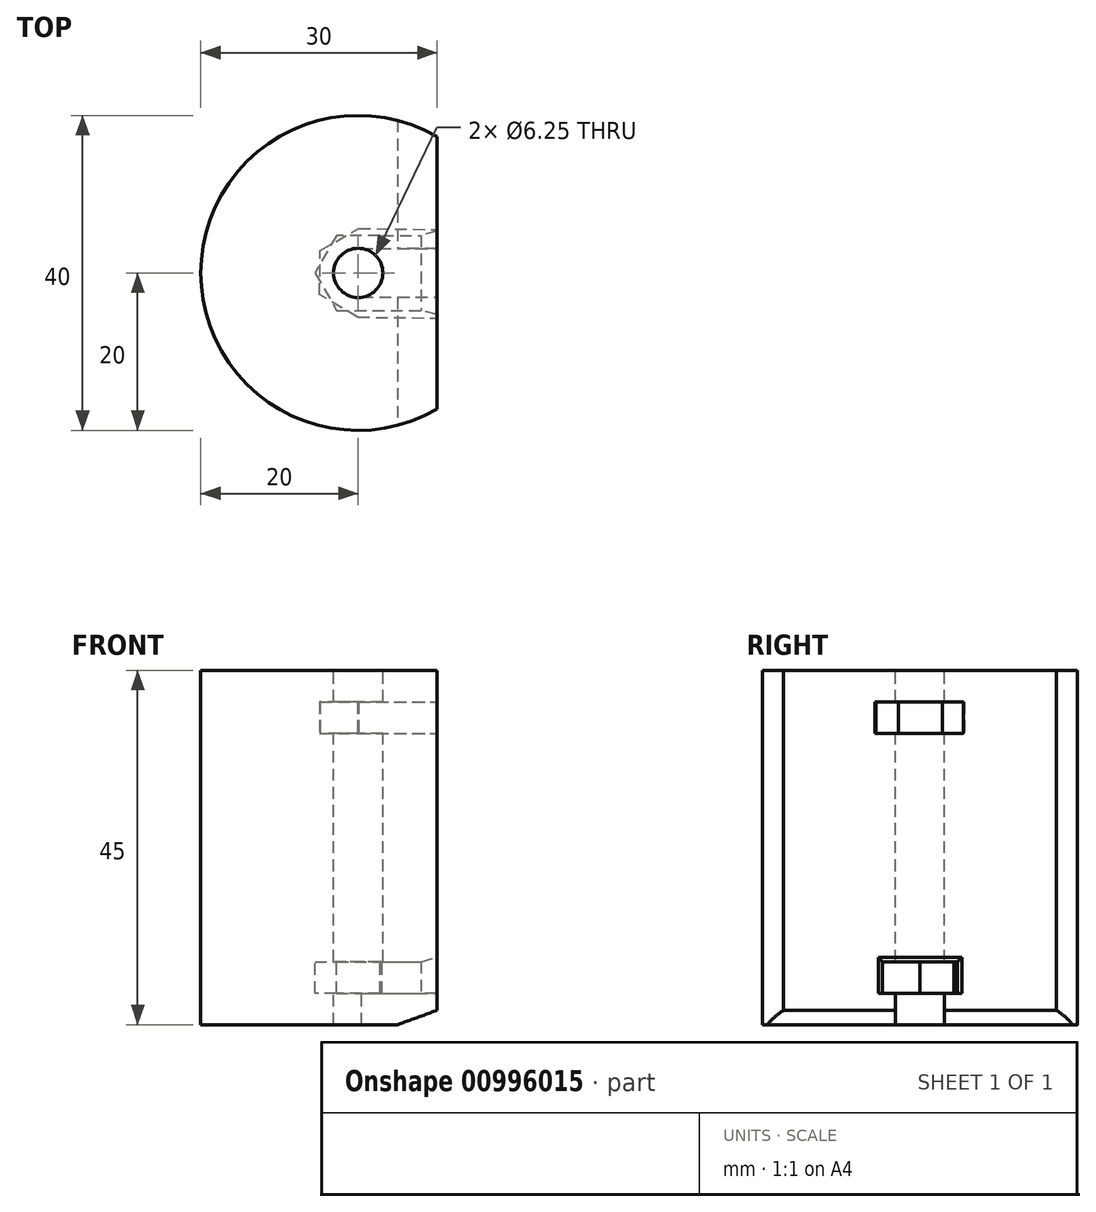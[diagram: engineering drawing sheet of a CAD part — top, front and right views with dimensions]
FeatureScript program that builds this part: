
annotation { "Feature Type Name" : "Feature", "Feature Type Description" : "" }
export const myFeature = defineFeature(function(context is Context, id is Id, definition is map)
    precondition{}
    {
        {
            var Q0;
            Q0=qCreatedBy(makeId("Top.planeOp"),FACE);
            var sketch = newSketch(context, id + "F0", { "sketchPlane" : qUnion([Q0])});
            skCircle(sketch, "E0", {"center": v(0, 0) * mm, "radius": 20 * mm});
            skSolve(sketch);
        }
        {
            var Q0;
            Q0=makeQuery(id+"F0.imprint","IMPRINT",FACE,{"disambiguationData":[TD([[makeQuery(id+"F0.imprint","IMPRINT",EDGE,{"derivedFrom":sQuery(id+"F0.wireOp",EDGE,"E0")}),1.0]])]});
            extrude(context, id + "F1", {"entities" : qUnion([Q0]), "endBound" : BoundingType.SYMMETRIC, "depth" : 45 * mm, "offsetDistance" : 25 * mm});
        }
        {
            var Q0;
            Q0=makeQuery(id+"F1.opExtrude","CAP_FACE",FACE,{"disambiguationData":[OSD([sQuery(id+"F0.wireOp",EDGE,"E0")])],"isStart":false});
            var sketch = newSketch(context, id + "F2", { "sketchPlane" : qUnion([Q0])});
            skCircle(sketch, "E1.cCircle", {"center": v(0, 0) * mm, "radius": 5.62 * mm, "construction": true});
            skLineSegment(sketch, "E1.0", {"start": v(4.9, 2.76) * mm, "end": v(4.84, -2.87) * mm});
            skLineSegment(sketch, "E1.1", {"start": v(4.84, -2.87) * mm, "end": v(-0.06, -5.62) * mm});
            skLineSegment(sketch, "E1.2", {"start": v(-0.06, -5.62) * mm, "end": v(-4.9, -2.76) * mm});
            skLineSegment(sketch, "E1.3", {"start": v(-4.9, -2.76) * mm, "end": v(-4.84, 2.87) * mm});
            skLineSegment(sketch, "E1.4", {"start": v(-4.84, 2.87) * mm, "end": v(0.06, 5.62) * mm});
            skLineSegment(sketch, "E1.5", {"start": v(0.06, 5.62) * mm, "end": v(4.9, 2.76) * mm});
            skLineSegment(sketch, "E2", {"start": v(0.06, 5.62) * mm, "end": v(49.1, 5.09) * mm});
            skLineSegment(sketch, "E3", {"start": v(-0.06, -5.62) * mm, "end": v(49.1, -6.16) * mm});
            skLineSegment(sketch, "E4", {"start": v(49.1, 5.09) * mm, "end": v(49.1, -6.16) * mm});
            skCircle(sketch, "E5", {"center": v(0, 0) * mm, "radius": 3.12 * mm});
            skLineSegment(sketch, "E6", {"start": v(10, 23.77) * mm, "end": v(10, -27.14) * mm});
            skLineSegment(sketch, "E7", {"start": v(10, -27.14) * mm, "end": v(69.74, 0) * mm});
            skLineSegment(sketch, "E8", {"start": v(69.74, 0) * mm, "end": v(10, 23.77) * mm});
            skSolve(sketch);
        }
        {
            var Q0;
            Q0=makeQuery(id+"F2.imprint","IMPRINT",FACE,{"disambiguationData":[TD([[makeQuery(id+"F2.imprint","IMPRINT",EDGE,{"derivedFrom":sQuery(id+"F2.wireOp",EDGE,"E1.0")}),-1.0]])]});
            var Q1;
            Q1=makeQuery(id+"F2.imprint","IMPRINT",FACE,{"disambiguationData":[TD([[makeQuery(id+"F2.imprint","IMPRINT",EDGE,{"derivedFrom":sQuery(id+"F2.wireOp",EDGE,"E1.0")}),1.0]])]});
            var Q2;
            {var subQ0=sQuery(id+"F2.wireOp",EDGE,"E4");Q2=makeQuery(id+"F2.imprint","IMPRINT",FACE,{"disambiguationData":[TD([[makeQuery(id+"F2.imprint","IMPRINT",EDGE,{"derivedFrom":subQ0}),-1.0]])]});}
            var Q3;
            Q3=makeQuery(id+"F2.imprint","IMPRINT",FACE,{"disambiguationData":[TD([[makeQuery(id+"F2.imprint","IMPRINT",EDGE,{"derivedFrom":sQuery(id+"F2.wireOp",EDGE,"E5")}),1.0]])]});
            extrude(context, id + "F3", {"entities" : qUnion([Q0, Q1, Q2, Q3]), "depth" : 4 * mm, "offsetDistance" : 25 * mm});
        }
        {
            var Q0;
            Q0=makeQuery(id+"F3.opExtrude","SWEPT_BODY",BODY,{"disambiguationData":[OSD([sQuery(id+"F2.wireOp",EDGE,"E1.0"),sQuery(id+"F2.wireOp",EDGE,"E1.1"),sQuery(id+"F2.wireOp",EDGE,"E1.2"),sQuery(id+"F2.wireOp",EDGE,"E1.3"),sQuery(id+"F2.wireOp",EDGE,"E1.4"),sQuery(id+"F2.wireOp",EDGE,"E1.5")])]});
            var Q1;
            Q1=makeQuery(id+"F1.opExtrude","CAP_FACE",FACE,{"disambiguationData":[OSD([sQuery(id+"F0.wireOp",EDGE,"E0")])],"isStart":true});
            transform(context, id + "F4", {"entities" : qUnion([Q0]), "transformType" : TransformType.TRANSLATION_DISTANCE, "transformDirection" : qUnion([Q1]), "distance" : 8 * mm, "makeCopy" : false});
        }
        {
            var Q0;
            Q0=makeQuery(id+"F2.imprint","IMPRINT",FACE,{"disambiguationData":[TD([[makeQuery(id+"F2.imprint","IMPRINT",EDGE,{"derivedFrom":sQuery(id+"F2.wireOp",EDGE,"E5")}),1.0]])]});
            var Q1;
            {var subQ0=sQuery(id+"F2.wireOp",EDGE,"E6");var subQ1=sQuery(id+"F2.wireOp",EDGE,"E2");var subQ2=makeQuery(id+"F2.imprint","INTERSECT",VERTEX,{"derivedFrom":[subQ1,subQ0]});Q1=makeQuery(id+"F2.imprint","IMPRINT",FACE,{"disambiguationData":[TD([[makeQuery(id+"F2.imprint","IMPRINT",EDGE,{"disambiguationData":[TD([[subQ2,-1.0]])],"derivedFrom":subQ1}),1.0]])]});}
            var Q2;
            {var subQ0=sQuery(id+"F2.wireOp",EDGE,"E6");var subQ1=sQuery(id+"F2.wireOp",EDGE,"E2");var subQ2=makeQuery(id+"F2.imprint","INTERSECT",VERTEX,{"derivedFrom":[subQ1,subQ0]});Q2=makeQuery(id+"F2.imprint","IMPRINT",FACE,{"disambiguationData":[TD([[makeQuery(id+"F2.imprint","IMPRINT",EDGE,{"disambiguationData":[TD([[subQ2,-1.0]])],"derivedFrom":subQ1}),-1.0]])]});}
            var Q3;
            {var subQ0=sQuery(id+"F2.wireOp",EDGE,"E6");var subQ1=sQuery(id+"F2.wireOp",EDGE,"E3");var subQ2=makeQuery(id+"F2.imprint","INTERSECT",VERTEX,{"derivedFrom":[subQ1,subQ0]});Q3=makeQuery(id+"F2.imprint","IMPRINT",FACE,{"disambiguationData":[TD([[makeQuery(id+"F2.imprint","IMPRINT",EDGE,{"disambiguationData":[TD([[subQ2,-1.0]])],"derivedFrom":subQ1}),-1.0]])]});}
            extrude(context, id + "F5", {"entities" : qUnion([Q0, Q1, Q2, Q3]), "operationType" : NewBodyOperationType.REMOVE, "endBound" : BoundingType.THROUGH_ALL, "oppositeDirection" : true, "depth" : 25 * mm, "offsetDistance" : 25 * mm});
        }
        {
            var Q0;
            Q0=makeQuery(id+"F3.opExtrude","SWEPT_BODY",BODY,{"disambiguationData":[OSD([sQuery(id+"F0.wireOp",EDGE,"E0"),sQuery(id+"F2.wireOp",EDGE,"E2"),sQuery(id+"F2.wireOp",EDGE,"E3"),sQuery(id+"F2.wireOp",EDGE,"E4")])]});
            deleteBodies(context, id + "F6", {"entities" : qUnion([Q0])});
        }
        {
            var Q0;
            Q0=makeQuery(id+"F3.opExtrude","SWEPT_BODY",BODY,{"disambiguationData":[OSD([sQuery(id+"F2.wireOp",EDGE,"E1.2"),sQuery(id+"F2.wireOp",EDGE,"E1.3"),sQuery(id+"F2.wireOp",EDGE,"E1.4"),sQuery(id+"F2.wireOp",EDGE,"E2"),sQuery(id+"F2.wireOp",EDGE,"E3"),sQuery(id+"F2.wireOp",EDGE,"E6")])]});
            var Q1;
            Q1=makeQuery(id+"F1.opExtrude","SWEPT_BODY",BODY,{"disambiguationData":[OSD([sQuery(id+"F0.wireOp",EDGE,"E0")])]});
            booleanBodies(context, id + "F7", {"operationType" : BooleanOperationType.SUBTRACTION, "tools" : qUnion([Q0]), "targets" : qUnion([Q1])});
        }
        {
            var Q0;
            Q0=makeQuery(id+"F1.opExtrude","CAP_FACE",FACE,{"disambiguationData":[OSD([sQuery(id+"F0.wireOp",EDGE,"E0")])],"isStart":true});
            var sketch = newSketch(context, id + "F8", { "sketchPlane" : qUnion([Q0])});
            skCircle(sketch, "E9.cCircle", {"center": v(0, 0) * mm, "radius": 5.5 * mm, "construction": true});
            skLineSegment(sketch, "E9.0", {"start": v(5.5, 0) * mm, "end": v(2.75, -4.76) * mm});
            skLineSegment(sketch, "E9.1", {"start": v(2.75, -4.76) * mm, "end": v(-2.75, -4.76) * mm});
            skLineSegment(sketch, "E9.2", {"start": v(-2.75, -4.76) * mm, "end": v(-5.5, 0) * mm});
            skLineSegment(sketch, "E9.3", {"start": v(-5.5, 0) * mm, "end": v(-2.75, 4.76) * mm});
            skLineSegment(sketch, "E9.4", {"start": v(-2.75, 4.76) * mm, "end": v(2.75, 4.76) * mm});
            skLineSegment(sketch, "E9.5", {"start": v(2.75, 4.76) * mm, "end": v(5.5, 0) * mm});
            skLineSegment(sketch, "E10", {"start": v(0, 0) * mm, "end": v(0, -21.96) * mm, "construction": true});
            skLineSegment(sketch, "E11", {"start": v(3, -21.96) * mm, "end": v(3, 0) * mm});
            skLineSegment(sketch, "E12.MirrorCS", {"start": v(-3, -21.96) * mm, "end": v(-3, 0) * mm});
            skLineSegment(sketch, "E13", {"start": v(2.75, 4.76) * mm, "end": v(22.17, 4.76) * mm});
            skLineSegment(sketch, "E14", {"start": v(2.75, -4.76) * mm, "end": v(22.86, -4.76) * mm});
            skLineSegment(sketch, "E15", {"start": v(22.86, -4.76) * mm, "end": v(22.17, 4.76) * mm});
            skSolve(sketch);
        }
        {
            var Q0;
            {var subQ0=sQuery(id+"F8.wireOp",EDGE,"E15");Q0=makeQuery(id+"F8.imprint","IMPRINT",FACE,{"disambiguationData":[TD([[makeQuery(id+"F8.imprint","IMPRINT",EDGE,{"derivedFrom":subQ0}),1.0]])]});}
            var Q1;
            {var subQ1=sQuery(id+"F8.wireOp",EDGE,"E9.5");Q1=makeQuery(id+"F8.imprint","IMPRINT",FACE,{"disambiguationData":[TD([[makeQuery(id+"F8.imprint","IMPRINT",EDGE,{"derivedFrom":subQ1}),1.0]])]});}
            var Q2;
            {var subQ0=sQuery(id+"F8.wireOp",EDGE,"E9.3");Q2=makeQuery(id+"F8.imprint","IMPRINT",FACE,{"disambiguationData":[TD([[makeQuery(id+"F8.imprint","IMPRINT",EDGE,{"derivedFrom":subQ0}),-1.0]])]});}
            var Q3;
            {var subQ6=sQuery(id+"F8.wireOp",EDGE,"E9.1");Q3=makeQuery(id+"F8.imprint","IMPRINT",FACE,{"disambiguationData":[TD([[makeQuery(id+"F8.imprint","IMPRINT",EDGE,{"derivedFrom":subQ6}),-1.0]])]});}
            extrude(context, id + "F9", {"entities" : qUnion([Q0, Q1, Q2, Q3]), "depth" : 4 * mm, "offsetDistance" : 25 * mm});
        }
        {
            var Q0;
            Q0=makeQuery(id+"F9.opExtrude","SWEPT_BODY",BODY,{"disambiguationData":[OSD([sQuery(id+"F0.wireOp",EDGE,"E0"),sQuery(id+"F2.wireOp",EDGE,"E5"),sQuery(id+"F8.wireOp",EDGE,"E9.0"),sQuery(id+"F8.wireOp",EDGE,"E9.1"),sQuery(id+"F8.wireOp",EDGE,"E9.2"),sQuery(id+"F8.wireOp",EDGE,"E9.3"),sQuery(id+"F8.wireOp",EDGE,"E9.4"),sQuery(id+"F8.wireOp",EDGE,"E11"),sQuery(id+"F8.wireOp",EDGE,"E13"),sQuery(id+"F8.wireOp",EDGE,"E14"),sQuery(id+"F8.wireOp",EDGE,"E15")])]});
            transform(context, id + "F10", {"entities" : qUnion([Q0]), "transformType" : TransformType.TRANSLATION_3D, "dx" : 0 * mm, "dy" : 0 * mm, "dz" : 8 * mm, "makeCopy" : false});
        }
        {
            var Q0;
            Q0=makeQuery(id+"F9.opExtrude","SWEPT_BODY",BODY,{"disambiguationData":[OSD([sQuery(id+"F0.wireOp",EDGE,"E0"),sQuery(id+"F2.wireOp",EDGE,"E5"),sQuery(id+"F8.wireOp",EDGE,"E9.0"),sQuery(id+"F8.wireOp",EDGE,"E9.1"),sQuery(id+"F8.wireOp",EDGE,"E9.2"),sQuery(id+"F8.wireOp",EDGE,"E9.3"),sQuery(id+"F8.wireOp",EDGE,"E9.4"),sQuery(id+"F8.wireOp",EDGE,"E11"),sQuery(id+"F8.wireOp",EDGE,"E13"),sQuery(id+"F8.wireOp",EDGE,"E14"),sQuery(id+"F8.wireOp",EDGE,"E15")])]});
            var Q1;
            Q1=makeQuery(id+"F1.opExtrude","SWEPT_BODY",BODY,{"disambiguationData":[OSD([sQuery(id+"F0.wireOp",EDGE,"E0")])]});
            booleanBodies(context, id + "F11", {"operationType" : BooleanOperationType.SUBTRACTION, "tools" : qUnion([Q0]), "targets" : qUnion([Q1])});
        }
        {
            var Q0;
            Q0=makeQuery(id+"F5.boolean.opBoolean","COPY",FACE,{"derivedFrom":makeQuery(id+"F5.opExtrude","SWEPT_FACE",FACE,{"disambiguationData":[OSD([sQuery(id+"F2.wireOp",EDGE,"E6")])]})});
            var sketch = newSketch(context, id + "F12", { "sketchPlane" : qUnion([Q0])});
            skLineSegment(sketch, "E16", {"start": v(0, 0) * mm, "end": v(0, -32.34) * mm, "construction": true});
            skPoint(sketch, "E16.endSnap0", {"position": v(0, -22.5) * mm});
            skLineSegment(sketch, "E17", {"start": v(3.1, 0) * mm, "end": v(3.1, -32.34) * mm});
            skLineSegment(sketch, "E18.MirrorCS", {"start": v(-3.1, 0) * mm, "end": v(-3.1, -32.34) * mm});
            skLineSegment(sketch, "E19", {"start": v(-3.1, 0) * mm, "end": v(3.1, 0) * mm});
            skLineSegment(sketch, "E20", {"start": v(-3.1, -32.34) * mm, "end": v(3.1, -32.34) * mm});
            skLineSegment(sketch, "E21", {"start": v(-3.1, -14.5) * mm, "end": v(3.1, -14.5) * mm});
            skSolve(sketch);
        }
        {
            var Q0;
            {var subQ0=sQuery(id+"F12.wireOp",EDGE,"E17");var subQ1=makeQuery(id+"F5.opExtrude","SWEPT_FACE",FACE,{"disambiguationData":[OSD([sQuery(id+"F2.wireOp",EDGE,"E6")])]});var subQ2=sQuery(id+"F0.wireOp",EDGE,"E0");var subQ3=makeQuery(id+"F5.boolean.opBoolean","INTERSECT",EDGE,{"derivedFrom":[makeQuery(id+"F1.opExtrude","CAP_FACE",FACE,{"disambiguationData":[OSD([subQ2])],"isStart":true}),subQ1]});var subQ4=makeQuery(id+"F12.imprint","INTERSECT",VERTEX,{"derivedFrom":[subQ3,subQ0]});Q0=makeQuery(id+"F12.imprint","IMPRINT",FACE,{"disambiguationData":[TD([[makeQuery(id+"F12.imprint","IMPRINT",EDGE,{"disambiguationData":[TD([[subQ4,-1.0]])],"derivedFrom":subQ3}),-1.0]])]});}
            extrude(context, id + "F13", {"entities" : qUnion([Q0]), "operationType" : NewBodyOperationType.REMOVE, "oppositeDirection" : true, "depth" : 10 * mm, "offsetDistance" : 25 * mm});
        }
        {
            var Q0;
            {var subQ0=sQuery(id+"F0.wireOp",EDGE,"E0");var subQ1=makeQuery(id+"F1.opExtrude","CAP_FACE",FACE,{"disambiguationData":[OSD([subQ0])],"isStart":true});var subQ2=makeQuery(id+"F5.opExtrude","SWEPT_FACE",FACE,{"disambiguationData":[OSD([sQuery(id+"F2.wireOp",EDGE,"E6")])]});Q0=makeQuery(id+"F13.boolean.opBoolean","SPLIT",EDGE,{"disambiguationData":[TD([makeQuery(id+"F13.opExtrude","SWEPT_FACE",FACE,{"disambiguationData":[OSD([sQuery(id+"F12.wireOp",EDGE,"E18.MirrorCS")])]})])],"derivedFrom":makeQuery(id+"F5.boolean.opBoolean","INTERSECT",EDGE,{"derivedFrom":[subQ1,subQ2]})});}
            var Q1;
            {var subQ0=sQuery(id+"F0.wireOp",EDGE,"E0");var subQ1=makeQuery(id+"F1.opExtrude","CAP_FACE",FACE,{"disambiguationData":[OSD([subQ0])],"isStart":true});var subQ2=makeQuery(id+"F5.opExtrude","SWEPT_FACE",FACE,{"disambiguationData":[OSD([sQuery(id+"F2.wireOp",EDGE,"E6")])]});Q1=makeQuery(id+"F13.boolean.opBoolean","SPLIT",EDGE,{"disambiguationData":[TD([makeQuery(id+"F13.opExtrude","SWEPT_FACE",FACE,{"disambiguationData":[OSD([sQuery(id+"F12.wireOp",EDGE,"E17")])]})])],"derivedFrom":makeQuery(id+"F5.boolean.opBoolean","INTERSECT",EDGE,{"derivedFrom":[subQ1,subQ2]})});}
            var Q2;
            Q2=makeQuery(id+"F5.boolean.opBoolean","COPY",EDGE,{"derivedFrom":makeQuery(id+"F5.opExtrude","CAP_EDGE",EDGE,{"disambiguationData":[OSD([sQuery(id+"F2.wireOp",EDGE,"E6")])],"isStart":true})});
            chamfer(context, id + "F14", {"entities" : qUnion([Q0, Q1, Q2]), "chamferType" : ChamferType.OFFSET_ANGLE, "width" : 5 * mm, "oppositeDirection" : false, "angle" : 20 * degree, "tangentPropagation" : true});
        }
        {
            var Q0;
            Q0=makeQuery(id+"F11.opBoolean","INTERSECT",EDGE,{"derivedFrom":[makeQuery(id+"F5.boolean.opBoolean","COPY",FACE,{"derivedFrom":makeQuery(id+"F5.opExtrude","SWEPT_FACE",FACE,{"disambiguationData":[OSD([sQuery(id+"F2.wireOp",EDGE,"E6")])]})}),makeQuery(id+"F9.opExtrude","CAP_FACE",FACE,{"disambiguationData":[OSD([sQuery(id+"F0.wireOp",EDGE,"E0"),sQuery(id+"F2.wireOp",EDGE,"E5"),sQuery(id+"F8.wireOp",EDGE,"E9.0"),sQuery(id+"F8.wireOp",EDGE,"E9.1"),sQuery(id+"F8.wireOp",EDGE,"E9.2"),sQuery(id+"F8.wireOp",EDGE,"E9.3"),sQuery(id+"F8.wireOp",EDGE,"E9.4"),sQuery(id+"F8.wireOp",EDGE,"E11"),sQuery(id+"F8.wireOp",EDGE,"E13"),sQuery(id+"F8.wireOp",EDGE,"E14"),sQuery(id+"F8.wireOp",EDGE,"E15")])],"isStart":true})]});
            var Q1;
            Q1=makeQuery(id+"F7.opBoolean","COPY",EDGE,{"derivedFrom":makeQuery(id+"F3.opExtrude","CAP_EDGE",EDGE,{"disambiguationData":[OSD([sQuery(id+"F2.wireOp",EDGE,"E6")])],"isStart":true})});
            var Q2;
            Q2=makeQuery(id+"F7.opBoolean","COPY",EDGE,{"derivedFrom":makeQuery(id+"F3.opExtrude","SWEPT_EDGE",EDGE,{"disambiguationData":[OSD([sQuery(id+"F2.wireOp",EDGE,"E2"),sQuery(id+"F2.wireOp",EDGE,"E6")])]})});
            var Q3;
            Q3=makeQuery(id+"F7.opBoolean","COPY",EDGE,{"derivedFrom":makeQuery(id+"F3.opExtrude","CAP_EDGE",EDGE,{"disambiguationData":[OSD([sQuery(id+"F2.wireOp",EDGE,"E6")])],"isStart":false})});
            var Q4;
            Q4=makeQuery(id+"F7.opBoolean","COPY",EDGE,{"derivedFrom":makeQuery(id+"F3.opExtrude","SWEPT_EDGE",EDGE,{"disambiguationData":[OSD([sQuery(id+"F2.wireOp",EDGE,"E3"),sQuery(id+"F2.wireOp",EDGE,"E6")])]})});
            var Q5;
            Q5=makeQuery(id+"F11.opBoolean","INTERSECT",EDGE,{"derivedFrom":[makeQuery(id+"F5.boolean.opBoolean","COPY",FACE,{"derivedFrom":makeQuery(id+"F5.opExtrude","SWEPT_FACE",FACE,{"disambiguationData":[OSD([sQuery(id+"F2.wireOp",EDGE,"E6")])]})}),makeQuery(id+"F9.opExtrude","SWEPT_FACE",FACE,{"disambiguationData":[OSD([sQuery(id+"F8.wireOp",EDGE,"E9.4"),sQuery(id+"F8.wireOp",EDGE,"E13")])]})]});
            var Q6;
            Q6=makeQuery(id+"F11.opBoolean","INTERSECT",EDGE,{"derivedFrom":[makeQuery(id+"F5.boolean.opBoolean","COPY",FACE,{"derivedFrom":makeQuery(id+"F5.opExtrude","SWEPT_FACE",FACE,{"disambiguationData":[OSD([sQuery(id+"F2.wireOp",EDGE,"E6")])]})}),makeQuery(id+"F9.opExtrude","SWEPT_FACE",FACE,{"disambiguationData":[OSD([sQuery(id+"F8.wireOp",EDGE,"E14")])]})]});
            chamfer(context, id + "F15", {"entities" : qUnion([Q0, Q1, Q2, Q3, Q4, Q5, Q6]), "chamferType" : ChamferType.OFFSET_ANGLE, "width" : 2 * mm, "oppositeDirection" : false, "angle" : 15 * degree, "tangentPropagation" : true});
        }
    });
